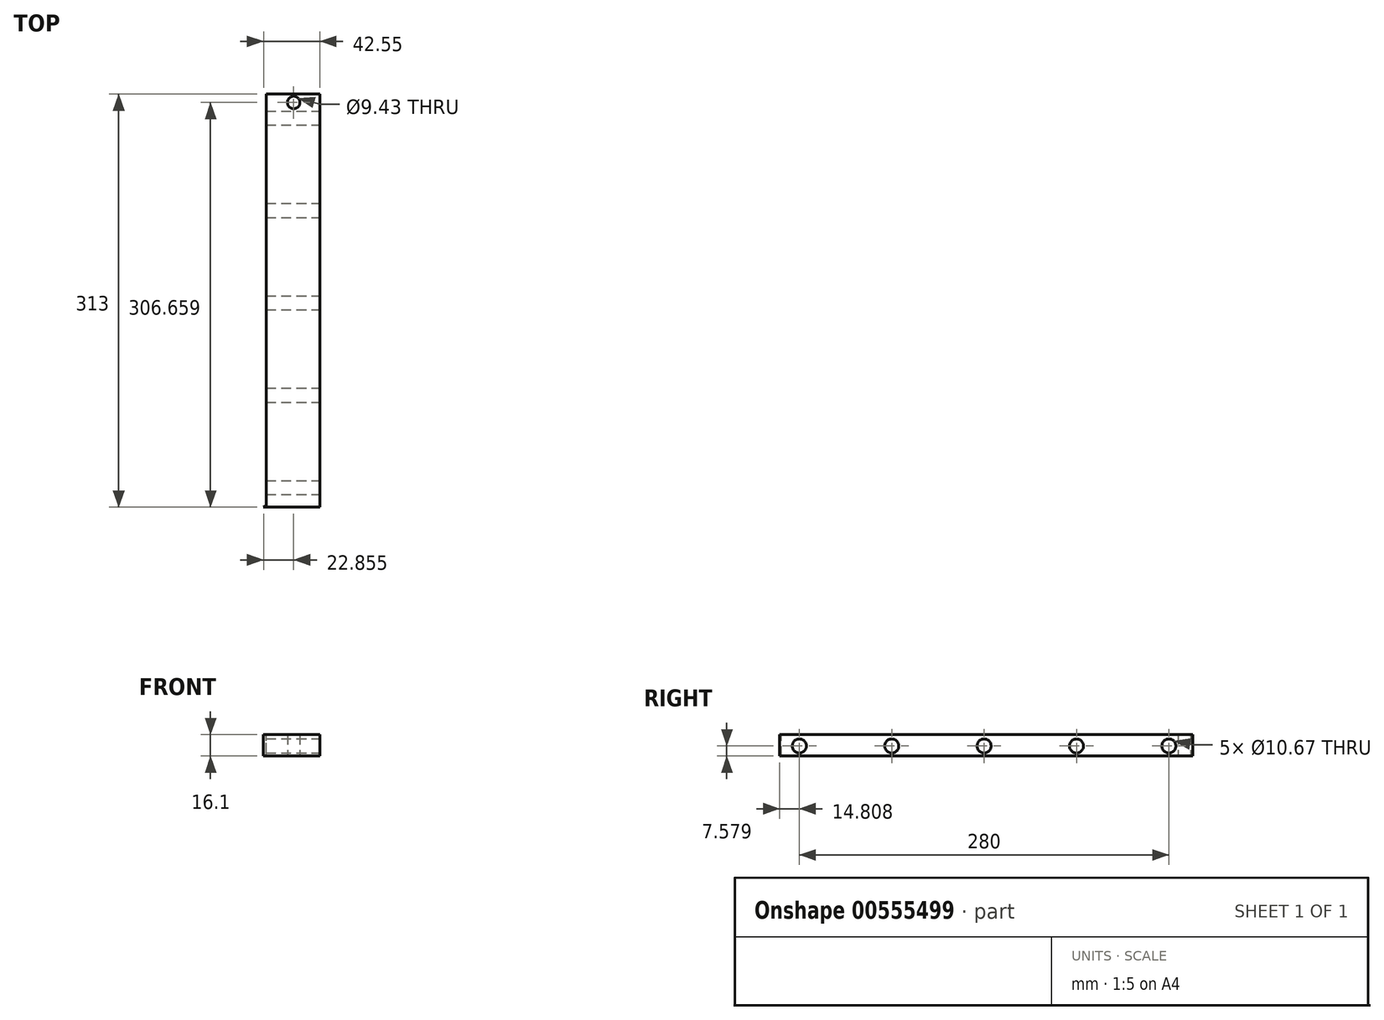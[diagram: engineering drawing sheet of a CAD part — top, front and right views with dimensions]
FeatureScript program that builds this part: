
annotation { "Feature Type Name" : "Feature", "Feature Type Description" : "" }
export const myFeature = defineFeature(function(context is Context, id is Id, definition is map)
    precondition{}
    {
        {
            var Q0;
            Q0=qCreatedBy(makeId("Front.planeOp"),FACE);
            var sketch = newSketch(context, id + "F0", { "sketchPlane" : qUnion([Q0])});
            skLineSegment(sketch, "E0.bottom", {"start": v(-35.43, 35.3) * mm, "end": v(27.95, 35.3) * mm});
            skLineSegment(sketch, "E0.top", {"start": v(-35.43, 19.2) * mm, "end": v(27.95, 19.2) * mm});
            skLineSegment(sketch, "E0.left", {"start": v(-35.43, 35.3) * mm, "end": v(-35.43, 19.2) * mm});
            skLineSegment(sketch, "E0.right", {"start": v(27.95, 35.3) * mm, "end": v(27.95, 19.2) * mm});
            skSolve(sketch);
        }
        {
            var Q0;
            Q0 = qSketchRegion(id + "F0", true);
            extrude(context, id + "F1", {"entities" : qUnion([Q0]), "depth" : 313 * mm, "offsetDistance" : 25 * mm});
        }
        {
            var Q0;
            Q0=makeQuery(id+"F1.opExtrude","SWEPT_FACE",FACE,{"disambiguationData":[OSD([sQuery(id+"F0.wireOp",EDGE,"E0.right")])]});
            var sketch = newSketch(context, id + "F2", { "sketchPlane" : qUnion([Q0])});
            skCircle(sketch, "E1", {"center": v(-18.2, 26.78) * mm, "radius": 5.34 * mm});
            skCircle(sketch, "E2.1.0.0", {"center": v(-88.2, 26.78) * mm, "radius": 5.34 * mm});
            skCircle(sketch, "E2.2.0.0", {"center": v(-158.2, 26.78) * mm, "radius": 5.34 * mm});
            skCircle(sketch, "E2.3.0.0", {"center": v(-228.2, 26.78) * mm, "radius": 5.34 * mm});
            skCircle(sketch, "E2.4.0.0", {"center": v(-298.2, 26.78) * mm, "radius": 5.34 * mm});
            skLineSegment(sketch, "E2.direction1", {"start": v(-18.2, 26.78) * mm, "end": v(-88.2, 26.78) * mm, "construction": true});
            skSolve(sketch);
        }
        {
            var Q0;
            Q0 = qSketchRegion(id + "F2", true);
            extrude(context, id + "F3", {"entities" : qUnion([Q0]), "operationType" : NewBodyOperationType.REMOVE, "endBound" : BoundingType.THROUGH_ALL, "oppositeDirection" : true, "depth" : 25 * mm, "offsetDistance" : 25 * mm});
        }
        {
            var Q0;
            Q0=makeQuery(id+"F1.opExtrude","SWEPT_FACE",FACE,{"disambiguationData":[OSD([sQuery(id+"F0.wireOp",EDGE,"E0.bottom")])]});
            var sketch = newSketch(context, id + "F4", { "sketchPlane" : qUnion([Q0])});
            skSolve(sketch);
        }
        {
            var Q0;
            Q0=makeQuery(id+"F1.opExtrude","SWEPT_FACE",FACE,{"disambiguationData":[OSD([sQuery(id+"F0.wireOp",EDGE,"E0.top")])]});
            var sketch = newSketch(context, id + "F5", { "sketchPlane" : qUnion([Q0])});
            skCircle(sketch, "E3", {"center": v(8.25, 6.34) * mm, "radius": 4.72 * mm});
            skSolve(sketch);
        }
        {
            var Q0;
            Q0 = qSketchRegion(id + "F5", true);
            extrude(context, id + "F6", {"entities" : qUnion([Q0]), "operationType" : NewBodyOperationType.REMOVE, "oppositeDirection" : true, "depth" : 25 * mm, "offsetDistance" : 25 * mm});
        }
        {
            var Q0;
            {var subQ0=sQuery(id+"F0.wireOp",EDGE,"E0.bottom");Q0=makeQuery(id+"F4.imprint","IMPRINT",FACE,{"disambiguationData":[TD([[makeQuery(id+"F4.imprint","IMPRINT",EDGE,{"derivedFrom":makeQuery(id+"F1.opExtrude","CAP_EDGE",EDGE,{"disambiguationData":[OSD([subQ0])],"isStart":true})}),-1.0]])]});}
            var sketch = newSketch(context, id + "F7", { "sketchPlane" : qUnion([Q0])});
            skLineSegment(sketch, "E4", {"start": v(-12.64, -311.83) * mm, "end": v(-12.64, 0) * mm});
            skLineSegment(sketch, "E5", {"start": v(-12.64, 0) * mm, "end": v(-35.14, 11.58) * mm});
            skLineSegment(sketch, "E6", {"start": v(-35.14, 11.58) * mm, "end": v(-57.63, 0) * mm});
            skLineSegment(sketch, "E7", {"start": v(-57.63, 0) * mm, "end": v(-81.67, -321.14) * mm});
            skLineSegment(sketch, "E8", {"start": v(-81.67, -321.14) * mm, "end": v(-34.22, -324.7) * mm});
            skLineSegment(sketch, "E9", {"start": v(-34.22, -324.7) * mm, "end": v(-12.64, -311.83) * mm});
            skSolve(sketch);
        }
        {
            var Q0;
            Q0 = qSketchRegion(id + "F7", true);
            extrude(context, id + "F8", {"entities" : qUnion([Q0]), "operationType" : NewBodyOperationType.REMOVE, "oppositeDirection" : true, "depth" : 25 * mm, "offsetDistance" : 25 * mm});
        }
        {
            var Q0;
            Q0 = qSketchRegion(id + "F5", true);
            extrude(context, id + "F9", {"entities" : qUnion([Q0]), "operationType" : NewBodyOperationType.REMOVE, "oppositeDirection" : true, "depth" : 25 * mm, "offsetDistance" : 25 * mm});
        }
    });
